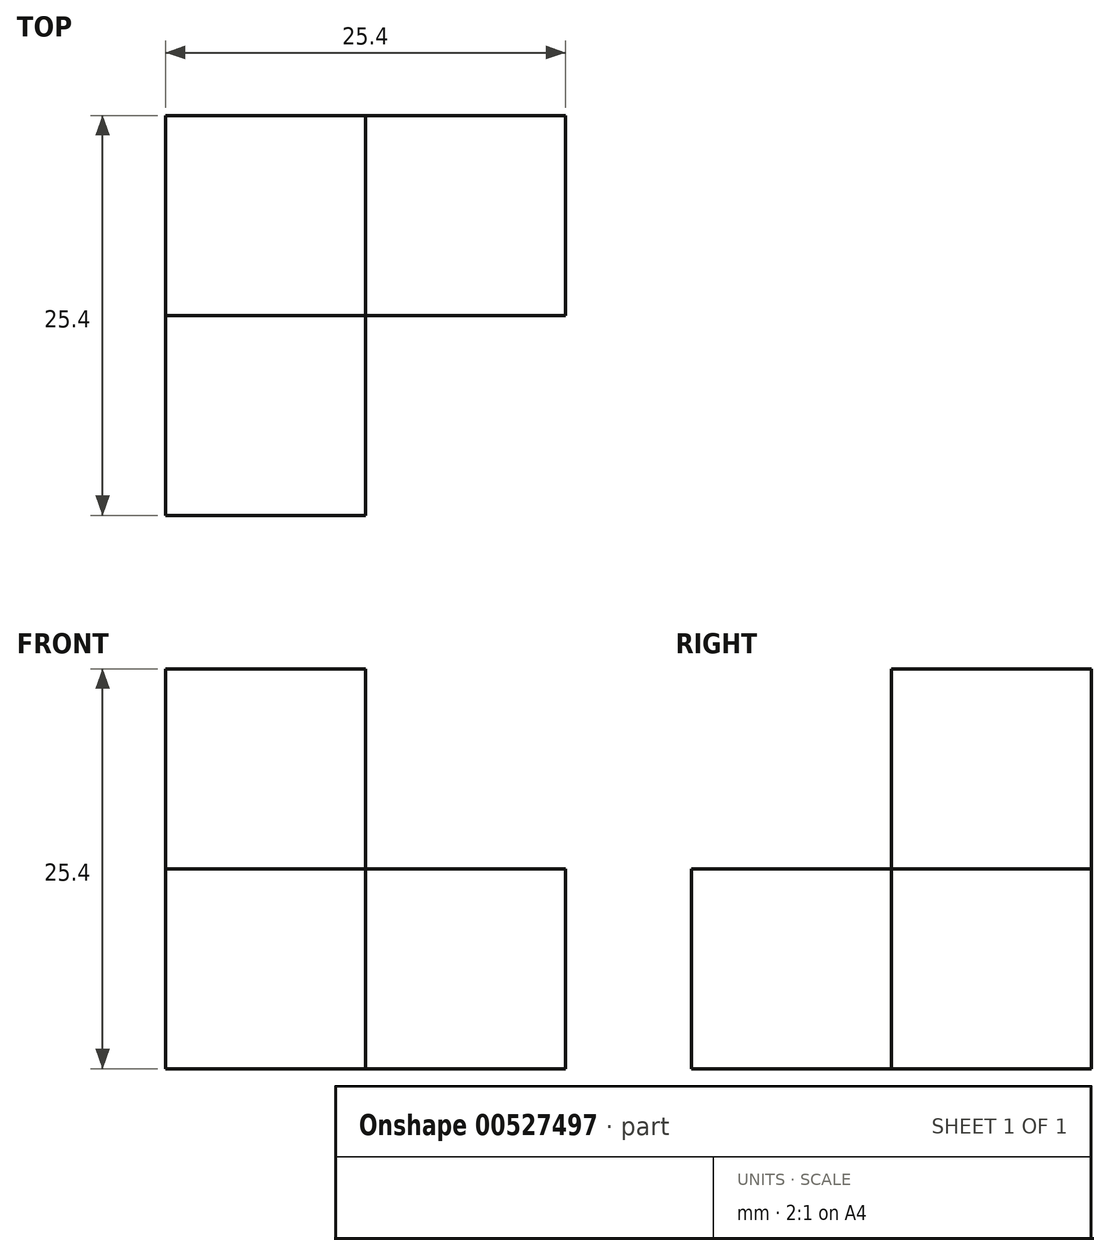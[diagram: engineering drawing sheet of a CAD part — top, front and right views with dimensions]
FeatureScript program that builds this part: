
annotation { "Feature Type Name" : "Feature", "Feature Type Description" : "" }
export const myFeature = defineFeature(function(context is Context, id is Id, definition is map)
    precondition{}
    {
        {
            var Q0;
            Q0=qCreatedBy(makeId("Top.planeOp"),FACE);
            var sketch = newSketch(context, id + "F0", { "sketchPlane" : qUnion([Q0])});
            skLineSegment(sketch, "E0.bottom", {"start": v(0, 0) * mm, "end": v(25.4, 0) * mm});
            skLineSegment(sketch, "E0.top", {"start": v(0, -12.7) * mm, "end": v(25.4, -12.7) * mm});
            skLineSegment(sketch, "E0.left", {"start": v(0, 0) * mm, "end": v(0, -12.7) * mm});
            skLineSegment(sketch, "E0.right", {"start": v(25.4, 0) * mm, "end": v(25.4, -12.7) * mm});
            skLineSegment(sketch, "E1.bottom", {"start": v(0, 0) * mm, "end": v(12.7, 0) * mm});
            skLineSegment(sketch, "E1.top", {"start": v(0, -25.4) * mm, "end": v(12.7, -25.4) * mm});
            skLineSegment(sketch, "E1.left", {"start": v(0, 0) * mm, "end": v(0, -25.4) * mm});
            skLineSegment(sketch, "E1.right", {"start": v(12.7, 0) * mm, "end": v(12.7, -25.4) * mm});
            skSolve(sketch);
        }
        {
            var Q0;
            Q0 = qSketchRegion(id + "F0", true);
            extrude(context, id + "F1", {"entities" : qUnion([Q0]), "depth" : 12.7 * mm, "offsetDistance" : 25.4 * mm});
        }
        {
            var Q0;
            Q0=makeQuery(id+"F1.opExtrude","CAP_FACE",FACE,{"disambiguationData":[OSD([sQuery(id+"F0.wireOp",EDGE,"E0.bottom"),sQuery(id+"F0.wireOp",EDGE,"E0.top"),sQuery(id+"F0.wireOp",EDGE,"E0.right"),sQuery(id+"F0.wireOp",EDGE,"E1.bottom"),sQuery(id+"F0.wireOp",EDGE,"E1.top"),sQuery(id+"F0.wireOp",EDGE,"E1.left"),sQuery(id+"F0.wireOp",EDGE,"E1.right")])],"isStart":false});
            var sketch = newSketch(context, id + "F2", { "sketchPlane" : qUnion([Q0])});
            skLineSegment(sketch, "E2.bottom", {"start": v(0, 0) * mm, "end": v(12.7, 0) * mm});
            skLineSegment(sketch, "E2.top", {"start": v(0, -12.7) * mm, "end": v(12.7, -12.7) * mm});
            skLineSegment(sketch, "E2.left", {"start": v(0, 0) * mm, "end": v(0, -12.7) * mm});
            skLineSegment(sketch, "E2.right", {"start": v(12.7, 0) * mm, "end": v(12.7, -12.7) * mm});
            skSolve(sketch);
        }
        {
            var Q0;
            Q0 = qSketchRegion(id + "F2", true);
            extrude(context, id + "F3", {"entities" : qUnion([Q0]), "operationType" : NewBodyOperationType.ADD, "depth" : 12.7 * mm, "offsetDistance" : 25.4 * mm});
        }
    });
